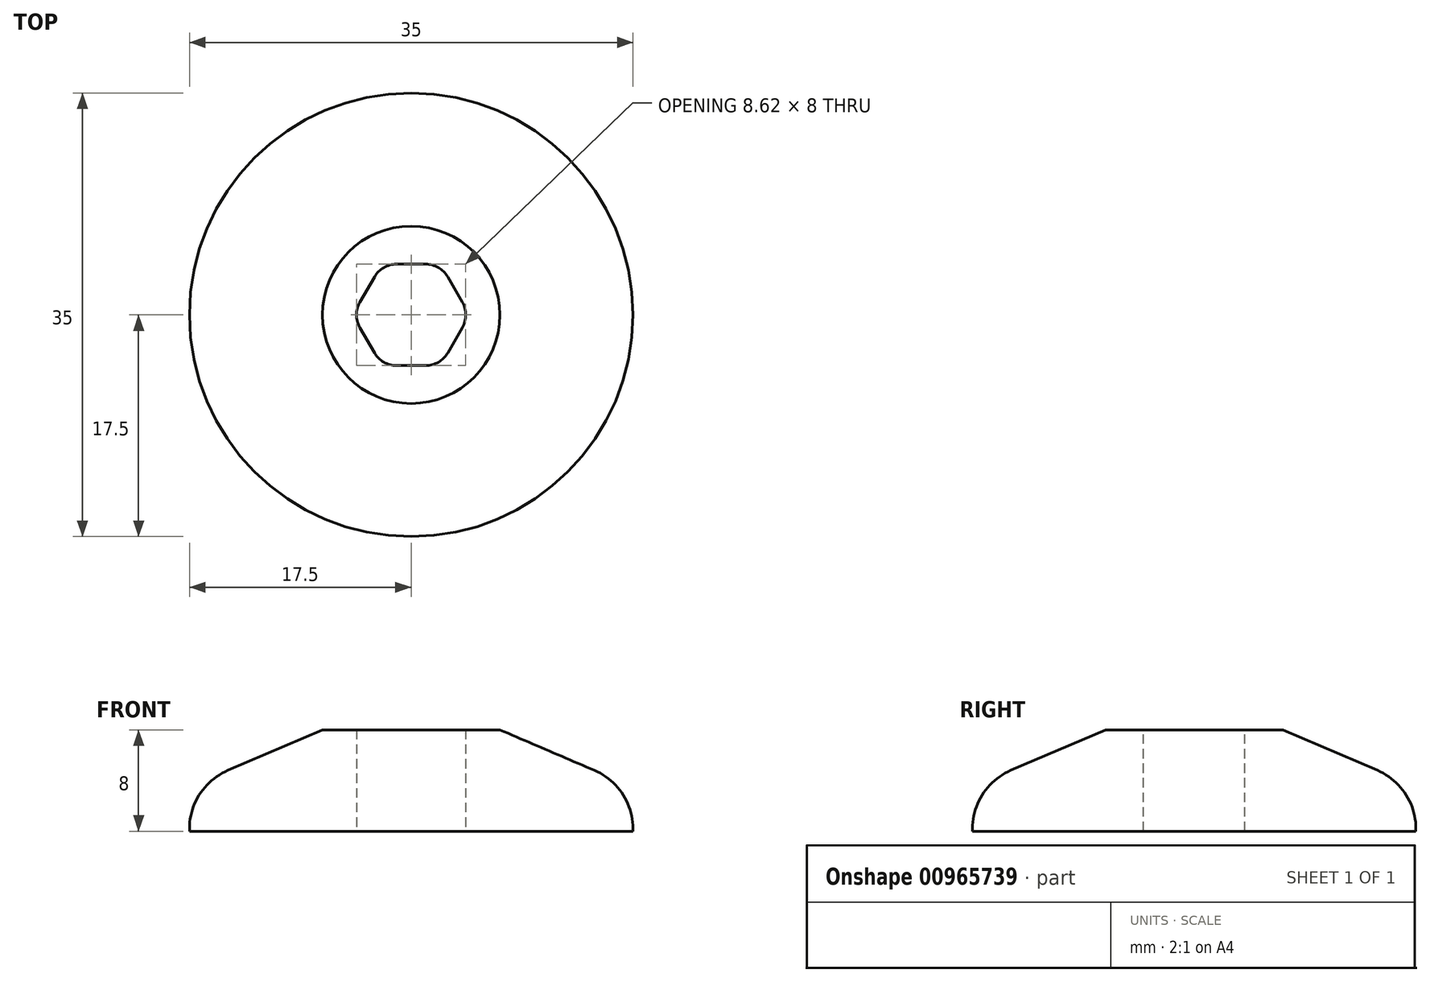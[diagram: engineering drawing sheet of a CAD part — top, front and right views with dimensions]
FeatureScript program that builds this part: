
annotation { "Feature Type Name" : "Feature", "Feature Type Description" : "" }
export const myFeature = defineFeature(function(context is Context, id is Id, definition is map)
    precondition{}
    {
        {
            var Q0;
            Q0=qCreatedBy(makeId("Front.planeOp"),FACE);
            var sketch = newSketch(context, id + "F0", { "sketchPlane" : qUnion([Q0])});
            skLineSegment(sketch, "E0", {"start": v(0, 0) * mm, "end": v(17.5, 0) * mm});
            skLineSegment(sketch, "E1", {"start": v(17.5, 0) * mm, "end": v(17.5, 0.2) * mm});
            skLineSegment(sketch, "E2", {"start": v(14.47, 4.8) * mm, "end": v(7, 8) * mm});
            skLineSegment(sketch, "E3", {"start": v(7, 8) * mm, "end": v(0, 8) * mm});
            skLineSegment(sketch, "E4", {"start": v(0, 8) * mm, "end": v(0, 0) * mm});
            skPoint(sketch, "E5.visualSharp", {"position": v(17.5, 3.5) * mm});
            skArc(sketch, "E5.filletArc", {"start": v(17.5, 0.2) * mm, "mid": v(16.67, 2.96) * mm, "end": v(14.47, 4.8) * mm});
            skLineSegment(sketch, "E6", {"start": v(0, 29.72) * mm, "end": v(0, -38.7) * mm, "construction": true});
            skSolve(sketch);
        }
        {
            var Q0;
            Q0 = qSketchRegion(id + "F0", true);
            var Q1;
            Q1=sQuery(id+"F0.wireOp",EDGE,"E6");
            revolve(context, id + "F1", {"surfaceOperationType" : NewSurfaceOperationType.NEW, "entities" : qUnion([Q0]), "axis" : qUnion([Q1]), "revolveType" : RevolveType.FULL});
        }
        {
            var Q0;
            Q0=makeQuery(id+"F1.opRevolve","SWEPT_FACE",FACE,{"disambiguationData":[OSD([sQuery(id+"F0.wireOp",EDGE,"E3")])]});
            var sketch = newSketch(context, id + "F2", { "sketchPlane" : qUnion([Q0])});
            skCircle(sketch, "E7.cCircle", {"center": v(0, 0) * mm, "radius": 4 * mm, "construction": true});
            skLineSegment(sketch, "E7.0", {"start": v(-2.3, 4) * mm, "end": v(2.3, 4) * mm});
            skLineSegment(sketch, "E7.1", {"start": v(2.3, 4) * mm, "end": v(4.62, 0) * mm});
            skLineSegment(sketch, "E7.2", {"start": v(4.62, 0) * mm, "end": v(2.3, -4) * mm});
            skLineSegment(sketch, "E7.3", {"start": v(2.3, -4) * mm, "end": v(-2.3, -4) * mm});
            skLineSegment(sketch, "E7.4", {"start": v(-2.3, -4) * mm, "end": v(-4.62, 0) * mm});
            skLineSegment(sketch, "E7.5", {"start": v(-4.62, 0) * mm, "end": v(-2.3, 4) * mm});
            skPoint(sketch, "E7.0.midPoint", {"position": v(0, 4) * mm});
            skSolve(sketch);
        }
        {
            var Q0;
            Q0 = qSketchRegion(id + "F2", true);
            extrude(context, id + "F3", {"entities" : qUnion([Q0]), "operationType" : NewBodyOperationType.REMOVE, "oppositeDirection" : true, "depth" : 25 * mm, "offsetDistance" : 25 * mm});
        }
        {
            var Q0;
            Q0=makeQuery(id+"F3.boolean.opBoolean","COPY",EDGE,{"derivedFrom":makeQuery(id+"F3.opExtrude","SWEPT_EDGE",EDGE,{"disambiguationData":[OSD([sQuery(id+"F2.wireOp",EDGE,"E7.0"),sQuery(id+"F2.wireOp",EDGE,"E7.5")])]})});
            var Q1;
            Q1=makeQuery(id+"F3.boolean.opBoolean","COPY",EDGE,{"derivedFrom":makeQuery(id+"F3.opExtrude","SWEPT_EDGE",EDGE,{"disambiguationData":[OSD([sQuery(id+"F2.wireOp",EDGE,"E7.4"),sQuery(id+"F2.wireOp",EDGE,"E7.5")])]})});
            var Q2;
            Q2=makeQuery(id+"F3.boolean.opBoolean","COPY",EDGE,{"derivedFrom":makeQuery(id+"F3.opExtrude","SWEPT_EDGE",EDGE,{"disambiguationData":[OSD([sQuery(id+"F2.wireOp",EDGE,"E7.0"),sQuery(id+"F2.wireOp",EDGE,"E7.1")])]})});
            var Q3;
            Q3=makeQuery(id+"F3.boolean.opBoolean","COPY",EDGE,{"derivedFrom":makeQuery(id+"F3.opExtrude","SWEPT_EDGE",EDGE,{"disambiguationData":[OSD([sQuery(id+"F2.wireOp",EDGE,"E7.1"),sQuery(id+"F2.wireOp",EDGE,"E7.2")])]})});
            var Q4;
            Q4=makeQuery(id+"F3.boolean.opBoolean","COPY",EDGE,{"derivedFrom":makeQuery(id+"F3.opExtrude","SWEPT_EDGE",EDGE,{"disambiguationData":[OSD([sQuery(id+"F2.wireOp",EDGE,"E7.3"),sQuery(id+"F2.wireOp",EDGE,"E7.4")])]})});
            var Q5;
            Q5=makeQuery(id+"F3.boolean.opBoolean","COPY",EDGE,{"derivedFrom":makeQuery(id+"F3.opExtrude","SWEPT_EDGE",EDGE,{"disambiguationData":[OSD([sQuery(id+"F2.wireOp",EDGE,"E7.2"),sQuery(id+"F2.wireOp",EDGE,"E7.3")])]})});
            fillet(context, id + "F4", {"entities" : qUnion([Q0, Q1, Q2, Q3, Q4, Q5]), "radius" : 2 * mm, "tangentPropagation" : true, "allowEdgeOverflow" : false});
        }
    });
